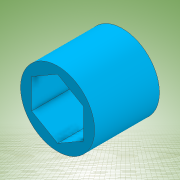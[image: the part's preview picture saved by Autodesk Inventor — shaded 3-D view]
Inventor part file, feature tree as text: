
AUTODESK INVENTOR PART (.ipt)
format: ipt  version: 2022 (Build 260153000, 153)  size: 122,368 bytes
history: native  units: mm
features: other x1, extrude x1, sketch x1
ambient origin geometry x8: Origin, YZ Plane, XZ Plane, XY Plane, X Axis, Y Axis, Z Axis, Center Point
bodies: Body1 (feature_tree)
feature tree (3):
  other  "Sólido1"
  extrude  "Extrusión1"  Depth=5.6mm
  sketch  "Boceto1"  dims[d0=8.0mm d1=5.6mm d2=7.0mm d3=0.0mm]
